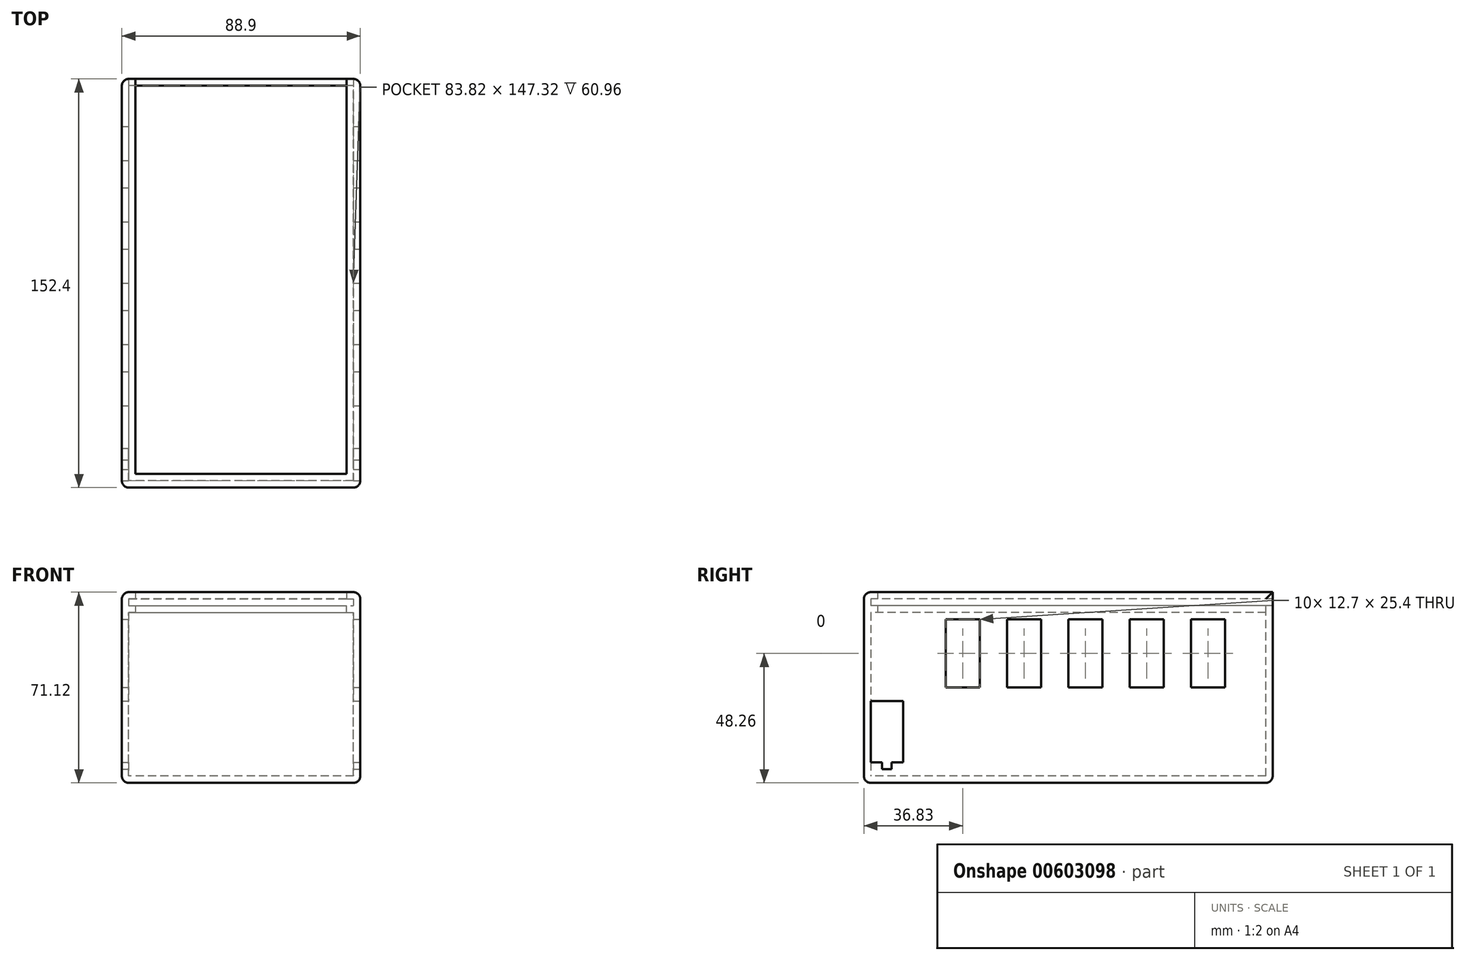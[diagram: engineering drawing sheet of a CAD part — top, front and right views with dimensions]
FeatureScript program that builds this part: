
annotation { "Feature Type Name" : "Feature", "Feature Type Description" : "" }
export const myFeature = defineFeature(function(context is Context, id is Id, definition is map)
    precondition{}
    {
        {
            var Q0;
            Q0=qCreatedBy(makeId("Right.planeOp"),FACE);
            var sketch = newSketch(context, id + "F0", { "sketchPlane" : qUnion([Q0])});
            skLineSegment(sketch, "E0.bottom", {"start": v(76.2, 35.56) * mm, "end": v(-76.2, 35.56) * mm});
            skLineSegment(sketch, "E0.top", {"start": v(76.2, -35.56) * mm, "end": v(-76.2, -35.56) * mm});
            skLineSegment(sketch, "E0.left", {"start": v(76.2, 35.56) * mm, "end": v(76.2, -35.56) * mm});
            skLineSegment(sketch, "E0.right", {"start": v(-76.2, 35.56) * mm, "end": v(-76.2, -35.56) * mm});
            skPoint(sketch, "E0.middle", {"position": v(0, 0) * mm});
            skSolve(sketch);
        }
        {
            var Q0;
            Q0 = qSketchRegion(id + "F0", true);
            extrude(context, id + "F1", {"entities" : qUnion([Q0]), "endBound" : BoundingType.SYMMETRIC, "depth" : 88.9 * mm, "offsetDistance" : 25.4 * mm});
        }
        {
            var Q0;
            Q0=makeQuery(id+"F1.opExtrude","SWEPT_FACE",FACE,{"disambiguationData":[OSD([sQuery(id+"F0.wireOp",EDGE,"E0.bottom")])]});
            var Q1;
            Q1=makeQuery(id+"F1.opExtrude","SWEPT_FACE",FACE,{"disambiguationData":[OSD([sQuery(id+"F0.wireOp",EDGE,"E0.left")])]});
            shell(context, id + "F2", {"entities" : qUnion([Q0, Q1]), "thickness" : 2.54 * mm});
        }
        {
            var Q0;
            {var subQ0=sQuery(id+"F0.wireOp",EDGE,"E0.right");var subQ1=sQuery(id+"F0.wireOp",EDGE,"E0.left");var subQ2=sQuery(id+"F0.wireOp",EDGE,"E0.top");var subQ3=sQuery(id+"F0.wireOp",EDGE,"E0.bottom");Q0=makeQuery(id+"F2.opShell","OFFSET_FACE",FACE,{"disambiguationData":[OSD([subQ3,subQ2,subQ1,subQ0]),TDD([makeQuery(id+"F1.opExtrude","CAP_FACE",FACE,{"disambiguationData":[OSD([subQ3,subQ2,subQ1,subQ0])],"isStart":true})])]});}
            var sketch = newSketch(context, id + "F3", { "sketchPlane" : qUnion([Q0])});
            skLineSegment(sketch, "E1.bottom", {"start": v(76.2, -33.02) * mm, "end": v(73.66, -33.02) * mm});
            skLineSegment(sketch, "E1.top", {"start": v(76.2, 30.48) * mm, "end": v(73.66, 30.48) * mm});
            skLineSegment(sketch, "E1.left", {"start": v(76.2, -33.02) * mm, "end": v(76.2, 30.48) * mm});
            skLineSegment(sketch, "E1.right", {"start": v(73.66, -33.02) * mm, "end": v(73.66, 30.48) * mm});
            skSolve(sketch);
        }
        {
            var Q0;
            Q0 = qSketchRegion(id + "F3", true);
            extrude(context, id + "F4", {"entities" : qUnion([Q0]), "operationType" : NewBodyOperationType.ADD, "endBound" : BoundingType.UP_TO_NEXT, "depth" : 25.4 * mm, "offsetDistance" : 25.4 * mm});
        }
        {
            var Q0;
            {var subQ0=sQuery(id+"F0.wireOp",EDGE,"E0.right");var subQ1=sQuery(id+"F0.wireOp",EDGE,"E0.left");var subQ2=sQuery(id+"F0.wireOp",EDGE,"E0.top");var subQ3=sQuery(id+"F0.wireOp",EDGE,"E0.bottom");Q0=makeQuery(id+"F2.opShell","OFFSET_FACE",FACE,{"disambiguationData":[OSD([subQ3,subQ2,subQ1,subQ0]),TDD([makeQuery(id+"F1.opExtrude","CAP_FACE",FACE,{"disambiguationData":[OSD([subQ3,subQ2,subQ1,subQ0])],"isStart":false})])]});}
            var sketch = newSketch(context, id + "F5", { "sketchPlane" : qUnion([Q0])});
            skLineSegment(sketch, "E2", {"start": v(-73.66, 30.48) * mm, "end": v(73.66, 30.48) * mm});
            skLineSegment(sketch, "E3", {"start": v(73.66, 30.48) * mm, "end": v(73.66, 27.94) * mm});
            skLineSegment(sketch, "E4", {"start": v(73.66, 27.94) * mm, "end": v(-73.66, 27.94) * mm});
            skLineSegment(sketch, "E5", {"start": v(-73.66, 27.94) * mm, "end": v(-73.66, 30.48) * mm});
            skLineSegment(sketch, "E6.bottom", {"start": v(-76.2, 35.56) * mm, "end": v(73.66, 35.56) * mm});
            skLineSegment(sketch, "E6.top", {"start": v(-76.2, 33.02) * mm, "end": v(73.66, 33.02) * mm});
            skLineSegment(sketch, "E6.left", {"start": v(-76.2, 35.56) * mm, "end": v(-76.2, 33.02) * mm});
            skLineSegment(sketch, "E6.right", {"start": v(73.66, 35.56) * mm, "end": v(73.66, 33.02) * mm});
            skSolve(sketch);
        }
        {
            var Q0;
            Q0 = qSketchRegion(id + "F5", true);
            extrude(context, id + "F6", {"entities" : qUnion([Q0]), "operationType" : NewBodyOperationType.ADD, "depth" : 2.54 * mm, "offsetDistance" : 25.4 * mm});
        }
        {
            var Q0;
            {var subQ0=sQuery(id+"F0.wireOp",EDGE,"E0.right");var subQ1=sQuery(id+"F0.wireOp",EDGE,"E0.left");var subQ2=sQuery(id+"F0.wireOp",EDGE,"E0.top");var subQ3=sQuery(id+"F0.wireOp",EDGE,"E0.bottom");Q0=makeQuery(id+"F2.opShell","OFFSET_FACE",FACE,{"disambiguationData":[OSD([subQ3,subQ2,subQ1,subQ0]),TDD([makeQuery(id+"F1.opExtrude","CAP_FACE",FACE,{"disambiguationData":[OSD([subQ3,subQ2,subQ1,subQ0])],"isStart":true})])]});}
            var sketch = newSketch(context, id + "F7", { "sketchPlane" : qUnion([Q0])});
            skLineSegment(sketch, "E7.bottom", {"start": v(73.66, 30.48) * mm, "end": v(-73.66, 30.48) * mm});
            skLineSegment(sketch, "E7.top", {"start": v(73.66, 27.94) * mm, "end": v(-73.66, 27.94) * mm});
            skLineSegment(sketch, "E7.left", {"start": v(73.66, 30.48) * mm, "end": v(73.66, 27.94) * mm});
            skLineSegment(sketch, "E7.right", {"start": v(-73.66, 30.48) * mm, "end": v(-73.66, 27.94) * mm});
            skPoint(sketch, "E8.oppositeSnap0", {"position": v(76.2, 33.02) * mm});
            skLineSegment(sketch, "E8.bottom", {"start": v(76.2, 35.56) * mm, "end": v(-73.66, 35.56) * mm});
            skLineSegment(sketch, "E8.top", {"start": v(76.2, 33.02) * mm, "end": v(-73.66, 33.02) * mm});
            skLineSegment(sketch, "E8.left", {"start": v(76.2, 35.56) * mm, "end": v(76.2, 33.02) * mm});
            skLineSegment(sketch, "E8.right", {"start": v(-73.66, 35.56) * mm, "end": v(-73.66, 33.02) * mm});
            skSolve(sketch);
        }
        {
            var Q0;
            Q0 = qSketchRegion(id + "F7", true);
            extrude(context, id + "F8", {"entities" : qUnion([Q0]), "operationType" : NewBodyOperationType.ADD, "depth" : 2.54 * mm, "offsetDistance" : 25.4 * mm});
        }
        {
            var Q0;
            Q0=makeQuery(id+"F2.opShell","OFFSET_FACE",FACE,{"disambiguationData":[OSD([sQuery(id+"F0.wireOp",EDGE,"E0.right")])]});
            var sketch = newSketch(context, id + "F9", { "sketchPlane" : qUnion([Q0])});
            skLineSegment(sketch, "E9.bottom", {"start": v(-39.37, 33.02) * mm, "end": v(39.37, 33.02) * mm});
            skLineSegment(sketch, "E9.top", {"start": v(-39.37, 35.56) * mm, "end": v(39.37, 35.56) * mm});
            skLineSegment(sketch, "E9.left", {"start": v(-39.37, 33.02) * mm, "end": v(-39.37, 35.56) * mm});
            skLineSegment(sketch, "E9.right", {"start": v(39.37, 33.02) * mm, "end": v(39.37, 35.56) * mm});
            skLineSegment(sketch, "E10.bottom", {"start": v(39.37, 27.94) * mm, "end": v(-39.37, 27.94) * mm});
            skLineSegment(sketch, "E10.top", {"start": v(39.37, 30.48) * mm, "end": v(-39.37, 30.48) * mm});
            skLineSegment(sketch, "E10.left", {"start": v(39.37, 27.94) * mm, "end": v(39.37, 30.48) * mm});
            skLineSegment(sketch, "E10.right", {"start": v(-39.37, 27.94) * mm, "end": v(-39.37, 30.48) * mm});
            skSolve(sketch);
        }
        {
            var Q0;
            Q0 = qSketchRegion(id + "F9", true);
            extrude(context, id + "F10", {"entities" : qUnion([Q0]), "operationType" : NewBodyOperationType.ADD, "depth" : 2.54 * mm, "offsetDistance" : 25.4 * mm});
        }
        {
            var Q0;
            {var subQ0=sQuery(id+"F0.wireOp",EDGE,"E0.top");var subQ1=sQuery(id+"F0.wireOp",EDGE,"E0.right");var subQ2=sQuery(id+"F0.wireOp",EDGE,"E0.left");var subQ3=sQuery(id+"F0.wireOp",EDGE,"E0.bottom");Q0=makeQuery(id+"F8.boolean.opBoolean","SPLIT",FACE,{"disambiguationData":[TD([makeQuery(id+"F2.opShell","OFFSET_FACE",FACE,{"disambiguationData":[OSD([subQ0])]})])],"derivedFrom":makeQuery(id+"F2.opShell","OFFSET_FACE",FACE,{"disambiguationData":[OSD([subQ3,subQ0,subQ2,subQ1]),TDD([makeQuery(id+"F1.opExtrude","CAP_FACE",FACE,{"disambiguationData":[OSD([subQ3,subQ0,subQ2,subQ1])],"isStart":true})])]})});}
            var sketch = newSketch(context, id + "F11", { "sketchPlane" : qUnion([Q0])});
            skLineSegment(sketch, "E11.bottom", {"start": v(-73.66, -27.94) * mm, "end": v(-61.54, -27.94) * mm});
            skLineSegment(sketch, "E11.top", {"start": v(-73.66, -5.08) * mm, "end": v(-61.54, -5.08) * mm});
            skLineSegment(sketch, "E11.left", {"start": v(-73.66, -27.94) * mm, "end": v(-73.66, -5.08) * mm});
            skLineSegment(sketch, "E11.right", {"start": v(-61.54, -27.94) * mm, "end": v(-61.54, -5.08) * mm});
            skLineSegment(sketch, "E12.bottom", {"start": v(-65.82, -25.4) * mm, "end": v(-69.38, -25.4) * mm});
            skLineSegment(sketch, "E12.top", {"start": v(-65.82, -30.48) * mm, "end": v(-69.38, -30.48) * mm});
            skLineSegment(sketch, "E12.left", {"start": v(-65.82, -25.4) * mm, "end": v(-65.82, -30.48) * mm});
            skLineSegment(sketch, "E12.right", {"start": v(-69.38, -25.4) * mm, "end": v(-69.38, -30.48) * mm});
            skPoint(sketch, "E12.middle", {"position": v(-67.6, -27.94) * mm});
            skLineSegment(sketch, "E13", {"start": v(-73.66, -33.02) * mm, "end": v(-73.66, 9.6) * mm});
            skSolve(sketch);
        }
        {
            var Q0;
            Q0 = qSketchRegion(id + "F11", true);
            extrude(context, id + "F12", {"entities" : qUnion([Q0]), "operationType" : NewBodyOperationType.REMOVE, "endBound" : BoundingType.SYMMETRIC, "oppositeDirection" : true, "depth" : 254 * mm, "offsetDistance" : 25.4 * mm});
        }
        {
            var Q0;
            Q0=makeQuery(id+"F1.opExtrude","SWEPT_EDGE",EDGE,{"disambiguationData":[OSD([sQuery(id+"F0.wireOp",EDGE,"E0.top"),sQuery(id+"F0.wireOp",EDGE,"E0.right")])]});
            var Q1;
            Q1=makeQuery(id+"F1.opExtrude","CAP_EDGE",EDGE,{"disambiguationData":[OSD([sQuery(id+"F0.wireOp",EDGE,"E0.top")])],"isStart":true});
            var Q2;
            Q2=makeQuery(id+"F1.opExtrude","CAP_EDGE",EDGE,{"disambiguationData":[OSD([sQuery(id+"F0.wireOp",EDGE,"E0.top")])],"isStart":false});
            var Q3;
            Q3=makeQuery(id+"F1.opExtrude","CAP_EDGE",EDGE,{"disambiguationData":[OSD([sQuery(id+"F0.wireOp",EDGE,"E0.right")])],"isStart":false});
            var Q4;
            Q4=makeQuery(id+"F1.opExtrude","CAP_EDGE",EDGE,{"disambiguationData":[OSD([sQuery(id+"F0.wireOp",EDGE,"E0.right")])],"isStart":true});
            var Q5;
            Q5=makeQuery(id+"F1.opExtrude","SWEPT_EDGE",EDGE,{"disambiguationData":[OSD([sQuery(id+"F0.wireOp",EDGE,"E0.top"),sQuery(id+"F0.wireOp",EDGE,"E0.left")])]});
            var Q6;
            Q6=makeQuery(id+"F1.opExtrude","CAP_EDGE",EDGE,{"disambiguationData":[OSD([sQuery(id+"F0.wireOp",EDGE,"E0.left")])],"isStart":false});
            var Q7;
            Q7=makeQuery(id+"F1.opExtrude","CAP_EDGE",EDGE,{"disambiguationData":[OSD([sQuery(id+"F0.wireOp",EDGE,"E0.left")])],"isStart":true});
            var Q8;
            Q8=makeQuery(id+"F1.opExtrude","SWEPT_EDGE",EDGE,{"disambiguationData":[OSD([sQuery(id+"F0.wireOp",EDGE,"E0.bottom"),sQuery(id+"F0.wireOp",EDGE,"E0.right")])]});
            var Q9;
            Q9=makeQuery(id+"F1.opExtrude","CAP_EDGE",EDGE,{"disambiguationData":[OSD([sQuery(id+"F0.wireOp",EDGE,"E0.bottom")])],"isStart":false});
            var Q10;
            Q10=makeQuery(id+"F1.opExtrude","CAP_EDGE",EDGE,{"disambiguationData":[OSD([sQuery(id+"F0.wireOp",EDGE,"E0.bottom")])],"isStart":true});
            fillet(context, id + "F13", {"entities" : qUnion([Q0, Q1, Q2, Q3, Q4, Q5, Q6, Q7, Q8, Q9, Q10]), "radius" : 2.54 * mm, "tangentPropagation" : true, "allowEdgeOverflow" : false});
        }
        {
            var Q0;
            Q0=makeQuery(id+"F1.opExtrude","CAP_FACE",FACE,{"disambiguationData":[OSD([sQuery(id+"F0.wireOp",EDGE,"E0.bottom"),sQuery(id+"F0.wireOp",EDGE,"E0.top"),sQuery(id+"F0.wireOp",EDGE,"E0.left"),sQuery(id+"F0.wireOp",EDGE,"E0.right")])],"isStart":false});
            var sketch = newSketch(context, id + "F14", { "sketchPlane" : qUnion([Q0])});
            skLineSegment(sketch, "E14", {"start": v(73.66, 0) * mm, "end": v(-73.66, 0) * mm});
            skLineSegment(sketch, "E15.bottom", {"start": v(-22.86, 0) * mm, "end": v(-10.16, 0) * mm});
            skLineSegment(sketch, "E15.top", {"start": v(-22.86, 25.4) * mm, "end": v(-10.16, 25.4) * mm});
            skLineSegment(sketch, "E15.left", {"start": v(-22.86, 0) * mm, "end": v(-22.86, 25.4) * mm});
            skLineSegment(sketch, "E15.right", {"start": v(-10.16, 0) * mm, "end": v(-10.16, 25.4) * mm});
            skLineSegment(sketch, "E16.bottom", {"start": v(22.86, 0) * mm, "end": v(35.56, 0) * mm});
            skLineSegment(sketch, "E16.top", {"start": v(22.86, 25.4) * mm, "end": v(35.56, 25.4) * mm});
            skLineSegment(sketch, "E16.left", {"start": v(22.86, 0) * mm, "end": v(22.86, 25.4) * mm});
            skLineSegment(sketch, "E16.right", {"start": v(35.56, 0) * mm, "end": v(35.56, 25.4) * mm});
            skLineSegment(sketch, "E17.bottom", {"start": v(45.72, 0) * mm, "end": v(58.42, 0) * mm});
            skLineSegment(sketch, "E17.top", {"start": v(45.72, 25.4) * mm, "end": v(58.42, 25.4) * mm});
            skLineSegment(sketch, "E17.left", {"start": v(45.72, 0) * mm, "end": v(45.72, 25.4) * mm});
            skLineSegment(sketch, "E17.right", {"start": v(58.42, 0) * mm, "end": v(58.42, 25.4) * mm});
            skLineSegment(sketch, "E18.bottom", {"start": v(0, 0) * mm, "end": v(12.7, 0) * mm});
            skLineSegment(sketch, "E18.top", {"start": v(0, 25.4) * mm, "end": v(12.7, 25.4) * mm});
            skLineSegment(sketch, "E18.left", {"start": v(0, 0) * mm, "end": v(0, 25.4) * mm});
            skLineSegment(sketch, "E18.right", {"start": v(12.7, 0) * mm, "end": v(12.7, 25.4) * mm});
            skLineSegment(sketch, "E19.bottom", {"start": v(-33.02, 0) * mm, "end": v(-45.72, 0) * mm});
            skLineSegment(sketch, "E19.top", {"start": v(-33.02, 25.4) * mm, "end": v(-45.72, 25.4) * mm});
            skLineSegment(sketch, "E19.left", {"start": v(-33.02, 0) * mm, "end": v(-33.02, 25.4) * mm});
            skLineSegment(sketch, "E19.right", {"start": v(-45.72, 0) * mm, "end": v(-45.72, 25.4) * mm});
            skSolve(sketch);
        }
        {
            var Q0;
            Q0 = qSketchRegion(id + "F14", true);
            extrude(context, id + "F15", {"entities" : qUnion([Q0]), "operationType" : NewBodyOperationType.REMOVE, "oppositeDirection" : true, "depth" : 254 * mm, "offsetDistance" : 25.4 * mm});
        }
    });
